# Revit family: 3D-AKE-00051097
name_source: partatom
category: Allgemeines Modell
units: mm (PartAtom-declared; Revit-internal decimal feet)

## family parameters
Arbeitsebenenbasiert = Nein
Beim Laden mit Abzugskörper schneiden = Nein
Bemaßung runder Anschluss = Durchmesser verwenden
Beschriftungsausrichtung beibehalten = Nein
Gemeinsam genutzt = Nein
Immer vertikal = Ja
Kann Basisbauteil für Bewehrung sein = Nein
Raumberechnungspunkt = Nein
Teiletyp = Normal

## types (1)
- Norm
    Abwicklungshöhe = 0
    Abwicklungslänge = 0
    Bauteilnummer = 3D-AKE-00051097
    Breite = 1125
    DocNumber = 3D-AKE-00051097
    Entstanden aus = 3D-AKE-00051049.ipt
    Ersatzteilkennung = nein
    Erstellungsdatum = 28.05.2024
    Folder = Produkte\Standardzeichnungen\
    Genehmigungsdatum Konstr. = 29.05.2024
    Gewicht = 1650,1 kg
    Höhe = 1592
    Kennung = Standardteil
    Konstruktionsstatus = 1
    Revisionsnummer = -
    Tiefe = 796
    Titel = Gastro HCGR-112-87-E R290
    VDS_Category = 3D-Konstruktion Bauteil
    Vorgabe-Ansicht = 0 mm  [stored 0 ft]

note: [stored X ft] marks values corroborated as IEEE doubles in the binary element streams (Revit-internal decimal feet)
